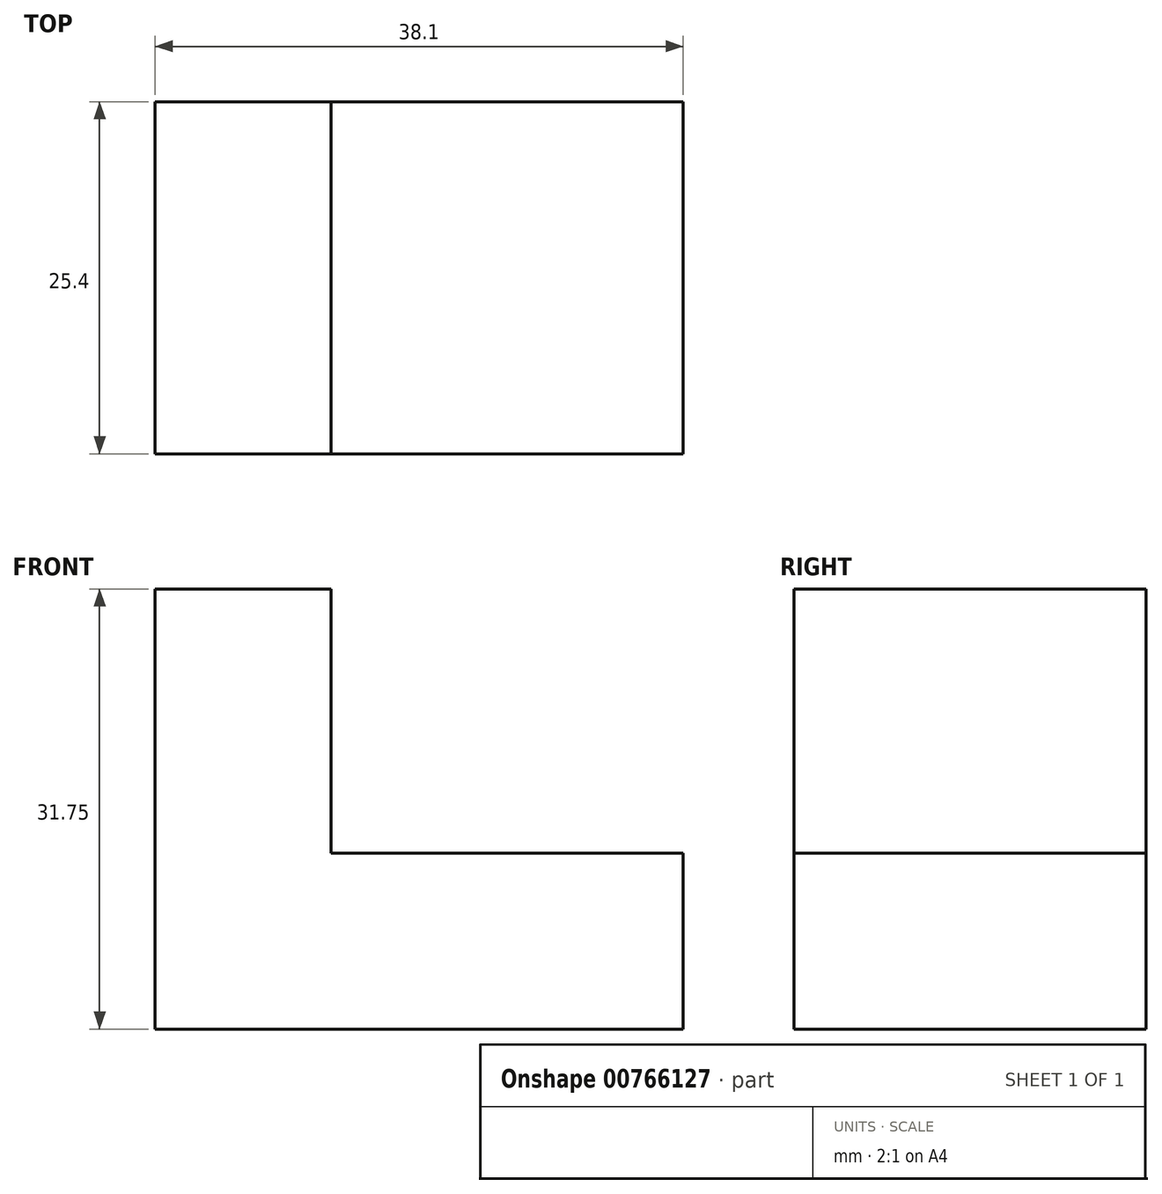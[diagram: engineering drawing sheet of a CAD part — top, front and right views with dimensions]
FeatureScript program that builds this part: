
annotation { "Feature Type Name" : "Feature", "Feature Type Description" : "" }
export const myFeature = defineFeature(function(context is Context, id is Id, definition is map)
    precondition{}
    {
        {
            var Q0;
            Q0=qCreatedBy(makeId("Front.planeOp"),FACE);
            var sketch = newSketch(context, id + "F0", { "sketchPlane" : qUnion([Q0])});
            skLineSegment(sketch, "E0", {"start": v(0, 0) * mm, "end": v(0, 31.75) * mm});
            skLineSegment(sketch, "E1", {"start": v(12.7, 31.75) * mm, "end": v(0, 31.75) * mm});
            skLineSegment(sketch, "E2", {"start": v(0, 31.75) * mm, "end": v(12.7, 31.75) * mm});
            skLineSegment(sketch, "E3", {"start": v(12.7, 31.75) * mm, "end": v(12.7, 12.7) * mm});
            skLineSegment(sketch, "E4", {"start": v(12.7, 12.7) * mm, "end": v(38.1, 12.7) * mm});
            skLineSegment(sketch, "E5", {"start": v(38.1, 12.7) * mm, "end": v(38.1, 0) * mm});
            skLineSegment(sketch, "E6", {"start": v(38.1, 0) * mm, "end": v(0, 0) * mm});
            skSolve(sketch);
        }
        {
            var Q0;
            Q0=makeQuery(id+"F0.imprint","IMPRINT",FACE,{"disambiguationData":[TD([[makeQuery(id+"F0.imprint","IMPRINT",EDGE,{"derivedFrom":sQuery(id+"F0.wireOp",EDGE,"E0")}),-1.0]])]});
            extrude(context, id + "F1", {"entities" : qUnion([Q0]), "depth" : 25.4 * mm, "offsetDistance" : 25.4 * mm});
        }
    });
